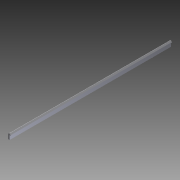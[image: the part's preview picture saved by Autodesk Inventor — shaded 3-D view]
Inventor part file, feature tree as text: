
AUTODESK INVENTOR PART (.ipt)
format: ipt  version: 2014 (Build 180170000, 170)  size: 94,720 bytes
history: native  units: in
note: dims shown in document units (in); Inventor stores cm internally (conversion verified against a paired STEP export)
features: fillet x1, other x1, imported_body x1
ambient origin geometry x8: Origin, YZ Plane, XZ Plane, XY Plane, X Axis, Y Axis, Z Axis, Center Point
bodies: Body1 (feature_tree)
feature tree (3):
  fillet  "Fillet1"  [1 undecoded]
  other  "BWC-T1-SS-11"
  imported_body  "Base1"
note: 1 required parameter value undecoded (feature->parameter linkage not recoverable at this tier; creation-order binding heuristic only, values carry confidence <= 0.55)
